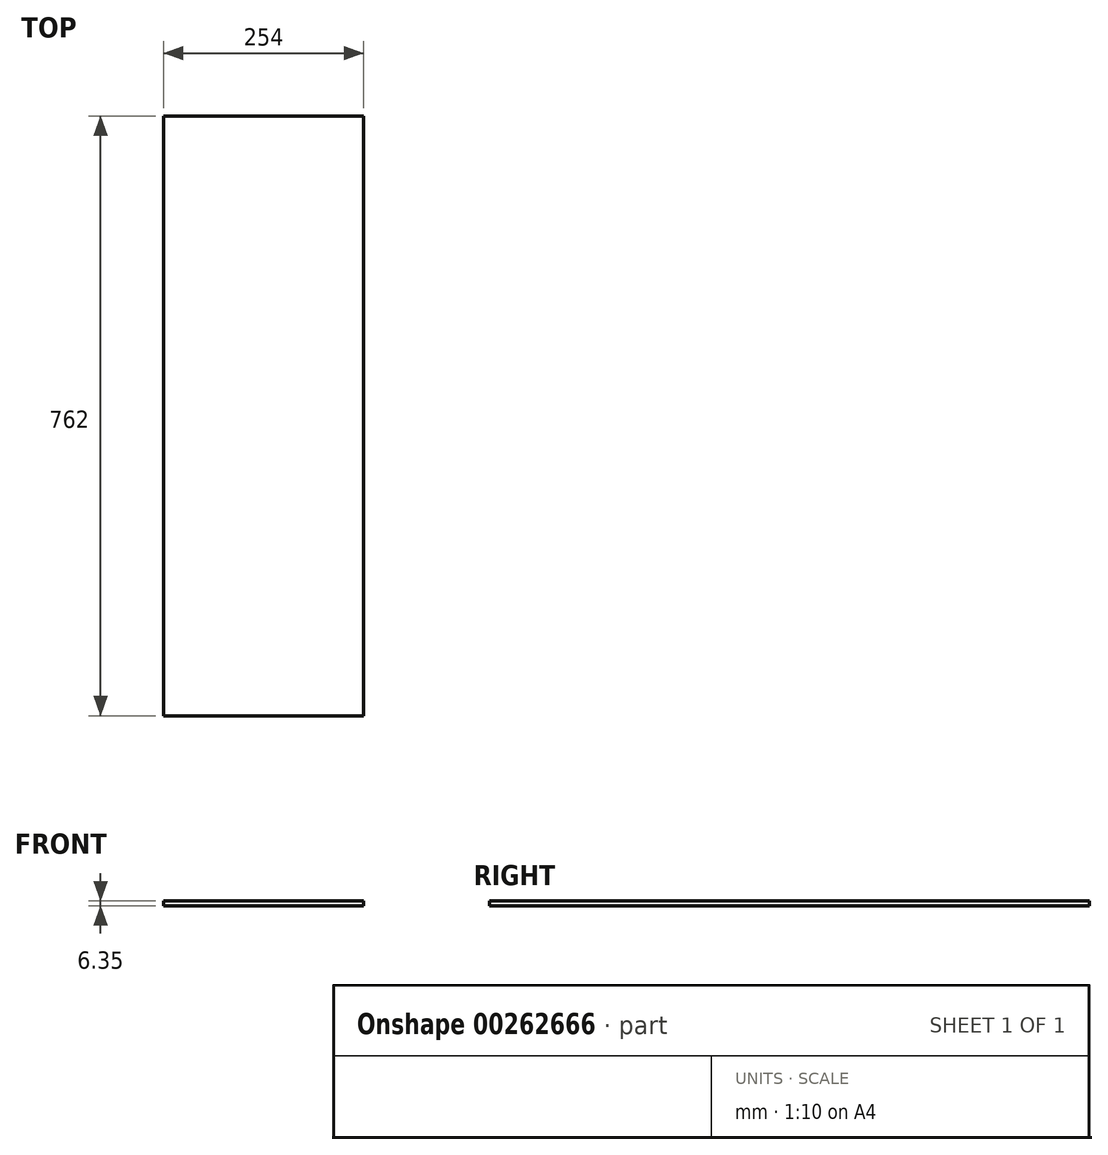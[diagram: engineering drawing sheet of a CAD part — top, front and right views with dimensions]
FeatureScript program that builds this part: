
annotation { "Feature Type Name" : "Feature", "Feature Type Description" : "" }
export const myFeature = defineFeature(function(context is Context, id is Id, definition is map)
    precondition{}
    {
        {
            var Q0;
            Q0=qCreatedBy(makeId("Top.planeOp"),FACE);
            var sketch = newSketch(context, id + "F0", { "sketchPlane" : qUnion([Q0])});
            skLineSegment(sketch, "E0.bottom", {"start": v(0, 0) * mm, "end": v(254, 0) * mm});
            skLineSegment(sketch, "E0.top", {"start": v(0, 762) * mm, "end": v(254, 762) * mm});
            skLineSegment(sketch, "E0.left", {"start": v(0, 0) * mm, "end": v(0, 762) * mm});
            skLineSegment(sketch, "E0.right", {"start": v(254, 0) * mm, "end": v(254, 762) * mm});
            skSolve(sketch);
        }
        {
            var Q0;
            Q0=makeQuery(id+"F0.imprint","IMPRINT",FACE,{"disambiguationData":[TD([[makeQuery(id+"F0.imprint","IMPRINT",EDGE,{"derivedFrom":sQuery(id+"F0.wireOp",EDGE,"E0.bottom")}),1.0]])]});
            extrude(context, id + "F1", {"entities" : qUnion([Q0]), "depth" : 6.35 * mm});
        }
    });
